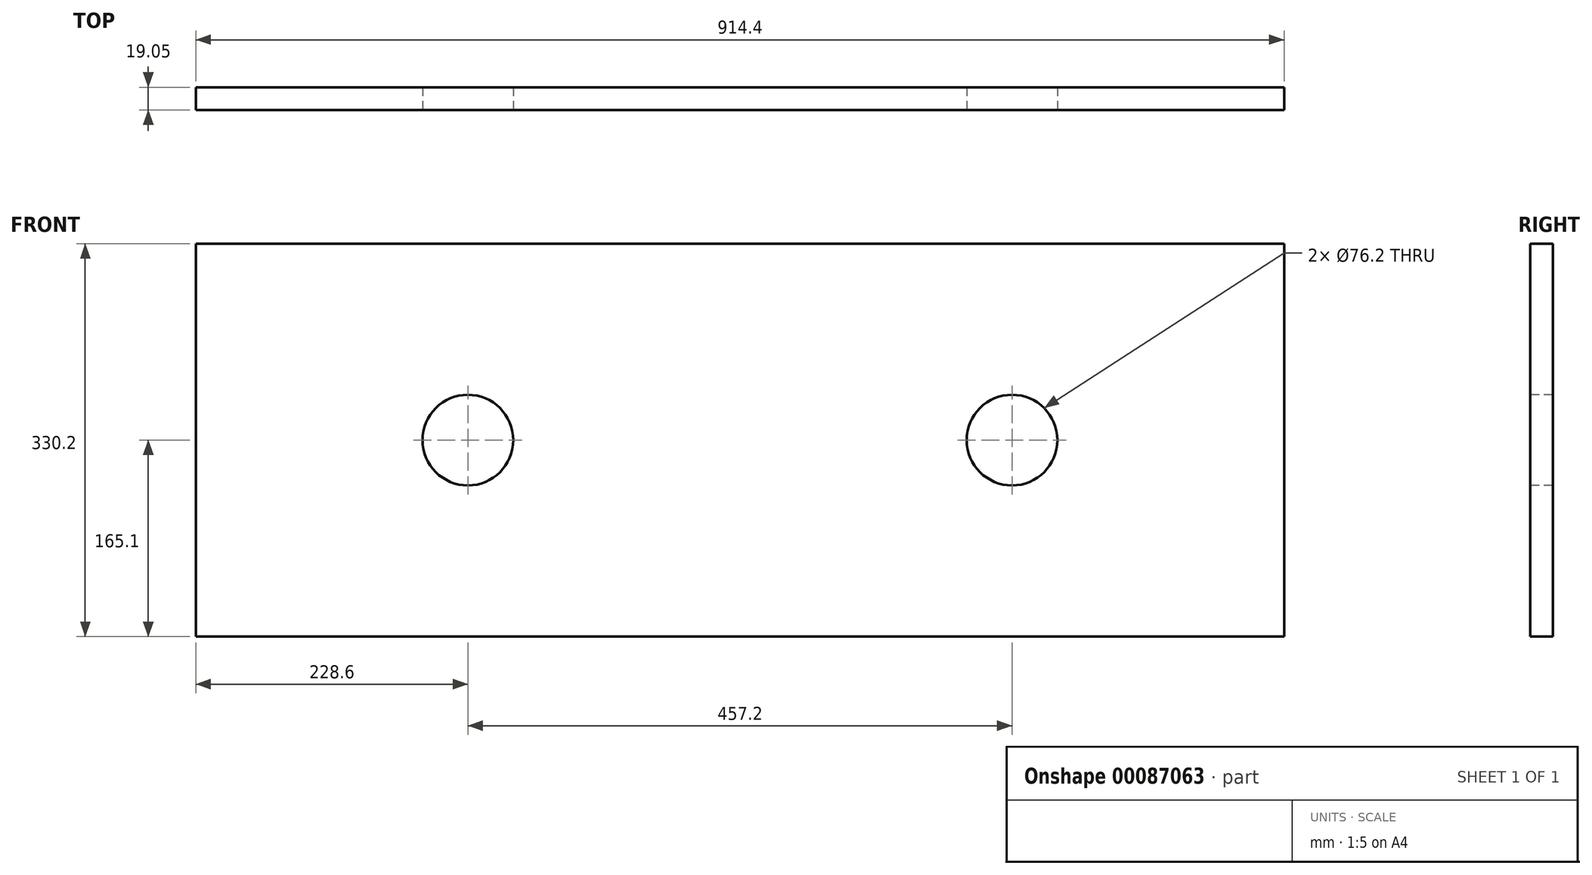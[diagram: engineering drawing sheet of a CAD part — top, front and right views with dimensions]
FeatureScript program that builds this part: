
annotation { "Feature Type Name" : "Feature", "Feature Type Description" : "" }
export const myFeature = defineFeature(function(context is Context, id is Id, definition is map)
    precondition{}
    {
        {
            var Q0;
            Q0=qCreatedBy(makeId("Front.planeOp"),FACE);
            var sketch = newSketch(context, id + "F0", { "sketchPlane" : qUnion([Q0])});
            skLineSegment(sketch, "E0.bottom", {"start": v(-457.2, 165.1) * mm, "end": v(457.2, 165.1) * mm});
            skLineSegment(sketch, "E0.top", {"start": v(-457.2, -165.1) * mm, "end": v(457.2, -165.1) * mm});
            skLineSegment(sketch, "E0.left", {"start": v(-457.2, 165.1) * mm, "end": v(-457.2, -165.1) * mm});
            skLineSegment(sketch, "E0.right", {"start": v(457.2, 165.1) * mm, "end": v(457.2, -165.1) * mm});
            skPoint(sketch, "E0.middle", {"position": v(0, 0) * mm});
            skSolve(sketch);
        }
        {
            var Q0;
            Q0=makeQuery(id+"F0.imprint","IMPRINT",FACE,{"disambiguationData":[TD([[makeQuery(id+"F0.imprint","IMPRINT",EDGE,{"derivedFrom":sQuery(id+"F0.wireOp",EDGE,"E0.bottom")}),-1.0]])]});
            extrude(context, id + "F1", {"entities" : qUnion([Q0]), "depth" : 19.05 * mm});
        }
        {
            var Q0;
            Q0=makeQuery(id+"F1.opExtrude","CAP_FACE",FACE,{"disambiguationData":[OSD([sQuery(id+"F0.wireOp",EDGE,"E0.bottom"),sQuery(id+"F0.wireOp",EDGE,"E0.top"),sQuery(id+"F0.wireOp",EDGE,"E0.left"),sQuery(id+"F0.wireOp",EDGE,"E0.right")])],"isStart":false});
            var sketch = newSketch(context, id + "F2", { "sketchPlane" : qUnion([Q0])});
            skLineSegment(sketch, "E1", {"start": v(-457.2, 165.1) * mm, "end": v(0, -165.1) * mm, "construction": true});
            skLineSegment(sketch, "E2", {"start": v(0, -165.1) * mm, "end": v(457.2, 165.1) * mm, "construction": true});
            skCircle(sketch, "E3", {"center": v(-228.6, 0) * mm, "radius": 38.1 * mm});
            skCircle(sketch, "E4", {"center": v(228.6, 0) * mm, "radius": 38.1 * mm});
            skSolve(sketch);
        }
        {
            var Q0;
            Q0=makeQuery(id+"F2.imprint","IMPRINT",FACE,{"disambiguationData":[TD([[makeQuery(id+"F2.imprint","IMPRINT",EDGE,{"derivedFrom":sQuery(id+"F2.wireOp",EDGE,"E3")}),1.0]])]});
            var Q1;
            Q1=makeQuery(id+"F2.imprint","IMPRINT",FACE,{"disambiguationData":[TD([[makeQuery(id+"F2.imprint","IMPRINT",EDGE,{"derivedFrom":sQuery(id+"F2.wireOp",EDGE,"E4")}),1.0]])]});
            extrude(context, id + "F3", {"entities" : qUnion([Q0, Q1]), "operationType" : NewBodyOperationType.REMOVE, "endBound" : BoundingType.THROUGH_ALL, "oppositeDirection" : true, "depth" : 25.4 * mm});
        }
    });
